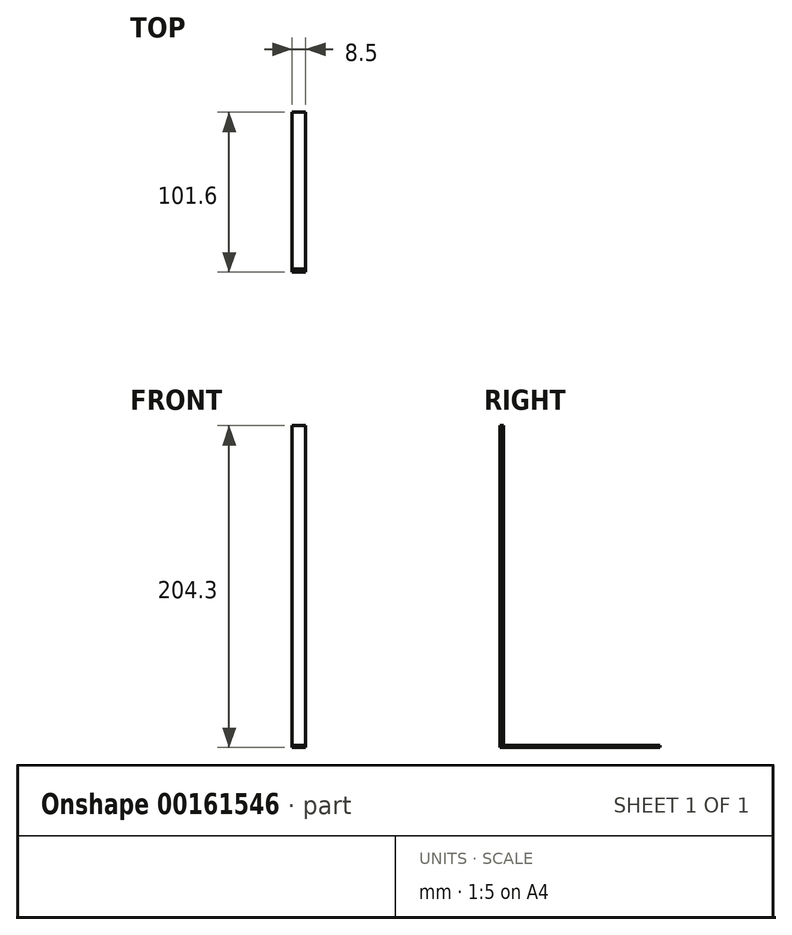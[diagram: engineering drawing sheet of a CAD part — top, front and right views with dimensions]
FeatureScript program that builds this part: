
annotation { "Feature Type Name" : "Feature", "Feature Type Description" : "" }
export const myFeature = defineFeature(function(context is Context, id is Id, definition is map)
    precondition{}
    {
        {
            var Q0;
            Q0=qCreatedBy(makeId("Top.planeOp"),FACE);
            var sketch = newSketch(context, id + "F0", { "sketchPlane" : qUnion([Q0])});
            skLineSegment(sketch, "E0.bottom", {"start": v(-32.92, 0) * mm, "end": v(-24.45, 0) * mm});
            skLineSegment(sketch, "E0.top", {"start": v(-32.92, 2.12) * mm, "end": v(-24.45, 2.12) * mm});
            skLineSegment(sketch, "E0.left", {"start": v(-32.92, 0) * mm, "end": v(-32.92, 2.12) * mm});
            skLineSegment(sketch, "E0.right", {"start": v(-24.45, 0) * mm, "end": v(-24.45, 2.12) * mm});
            skSolve(sketch);
        }
        {
            var Q0;
            Q0=makeQuery(id+"F0.imprint","IMPRINT",FACE,{"disambiguationData":[TD([[makeQuery(id+"F0.imprint","IMPRINT",EDGE,{"derivedFrom":sQuery(id+"F0.wireOp",EDGE,"E0.bottom")}),1.0]])]});
            extrude(context, id + "F1", {"entities" : qUnion([Q0]), "depth" : 203.2 * mm});
        }
        {
            var Q0;
            Q0=qCreatedBy(makeId("Front.planeOp"),FACE);
            var sketch = newSketch(context, id + "F2", { "sketchPlane" : qUnion([Q0])});
            skLineSegment(sketch, "E1.bottom", {"start": v(-32.94, 0) * mm, "end": v(-24.44, 0) * mm});
            skLineSegment(sketch, "E1.top", {"start": v(-32.94, -1.1) * mm, "end": v(-24.44, -1.1) * mm});
            skLineSegment(sketch, "E1.left", {"start": v(-32.94, 0) * mm, "end": v(-32.94, -1.1) * mm});
            skLineSegment(sketch, "E1.right", {"start": v(-24.44, 0) * mm, "end": v(-24.44, -1.1) * mm});
            skSolve(sketch);
        }
        {
            var Q0;
            Q0=makeQuery(id+"F2.imprint","IMPRINT",FACE,{"disambiguationData":[TD([[makeQuery(id+"F2.imprint","IMPRINT",EDGE,{"derivedFrom":sQuery(id+"F2.wireOp",EDGE,"E1.bottom")}),-1.0]])]});
            extrude(context, id + "F3", {"entities" : qUnion([Q0]), "oppositeDirection" : true, "depth" : 101.6 * mm});
        }
    });
